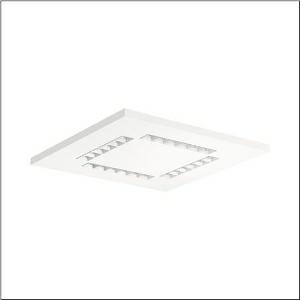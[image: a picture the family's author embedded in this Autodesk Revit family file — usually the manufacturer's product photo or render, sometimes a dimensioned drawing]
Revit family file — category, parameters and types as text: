
# Revit family: silica_21_square_51mx6ndu44w
name_source: partatom
category: Lighting Fixtures
units: mm (PartAtom-declared; Revit-internal decimal feet)

## family parameters
Cut with Voids When Loaded = No
Host = Face
Light Source = No
Part Type = Normal
Room Calculation Point = No
Round Connector Dimension = Use Diameter
Shared = No

## types (1)
- --- (1 x LED, 4600 lm, 27 W, 4000K)
    Apparent Load = 27 VA
    CIE Flux Codes = 83 98 100 100 100
    Color Rendering = 80
    Color Temperature = 4000K
    Default Elevation = 1800 mm
    Description = Silica 21 Square, office luminaire, primary light control with lens, of PMMA, primary anti-glare with reflector, of PC, white, CAT 2 (L<= 3000cd/m²), light emission: direct distribution, primary light characteristic: symmetric, installation type: lay-in mounting, LED, rated luminous flux: 4.600lm, luminous efficacy: 170lm/W, light colour: 840, colour temperature: 4000K, control gear: DALI 2, with terminal, 5-pole, mains connection: 220..240V, AC, 50/60Hz, rated input power: 27W, luminaire housing, of aluminium, traffic white (RAL 9016), module: M625, length: 622mm, width: 622mm, height: 32mm, protection rating (complete): IP20, insulation class (complete): insulation class I (protective earthing), certification: CE, ENEC, VDE, permissible operating ambient temperature: 0..+35°C, standard: EN 50419, packaging unit: 1 piece
    Height = 0 mm  [stored 0 ft]
    Lamp = 1 x LED
    Lamp Light Flux = 4600 lm
    Lamp Power = 27 W
    Lamp count = 1
    Length = 622 mm
    Luminous efficacy = 170 lm/W
    Manufacturer = Siteco
    ModVariant = No
    Model = 51MX6NDU44W
    Mounting Place = Ceiling
    Mounting Type = Recessed
    Number of Poles = 1
    OnlyDefault = Yes
    Power Factor = 1
    Product Name = Silica 21 Square
    Product group = office luminaire | ceiling recessed
    ProductGroupID = 400
    Protection Class = Protection class I
    Protection Degree = IP 20
    RLX_Detail_Level = 1
    RLX_Emergency_Light_Flux = 0 lm
    RLX_Emergency_Type = 0
    RLX_Emergency_Type_DB = No
    RlxData = <blob elided: 18981 chars, md5=9ae46f7d>
    Socket = socket
    Standby Power = 0 W
    System Light Flux = 4600 lm
    System Power = 27 W
    Type Comments = factory setting: luminous flux: 100 % | dim-lin: 254 | 366 mA
    Type Image = l_1275224.jpg
    URL = http://relux.com
    VarID = @adj_088407
    Voltage = 0 V
    Weight = 0.00 kg
    Width = 622 mm

note: [stored X ft] marks values corroborated as IEEE doubles in the binary element streams (Revit-internal decimal feet)

## geometry (parser evidence)
native form markers: Blend x4, Sweep x11
no freeform markers — native parametric forms only
